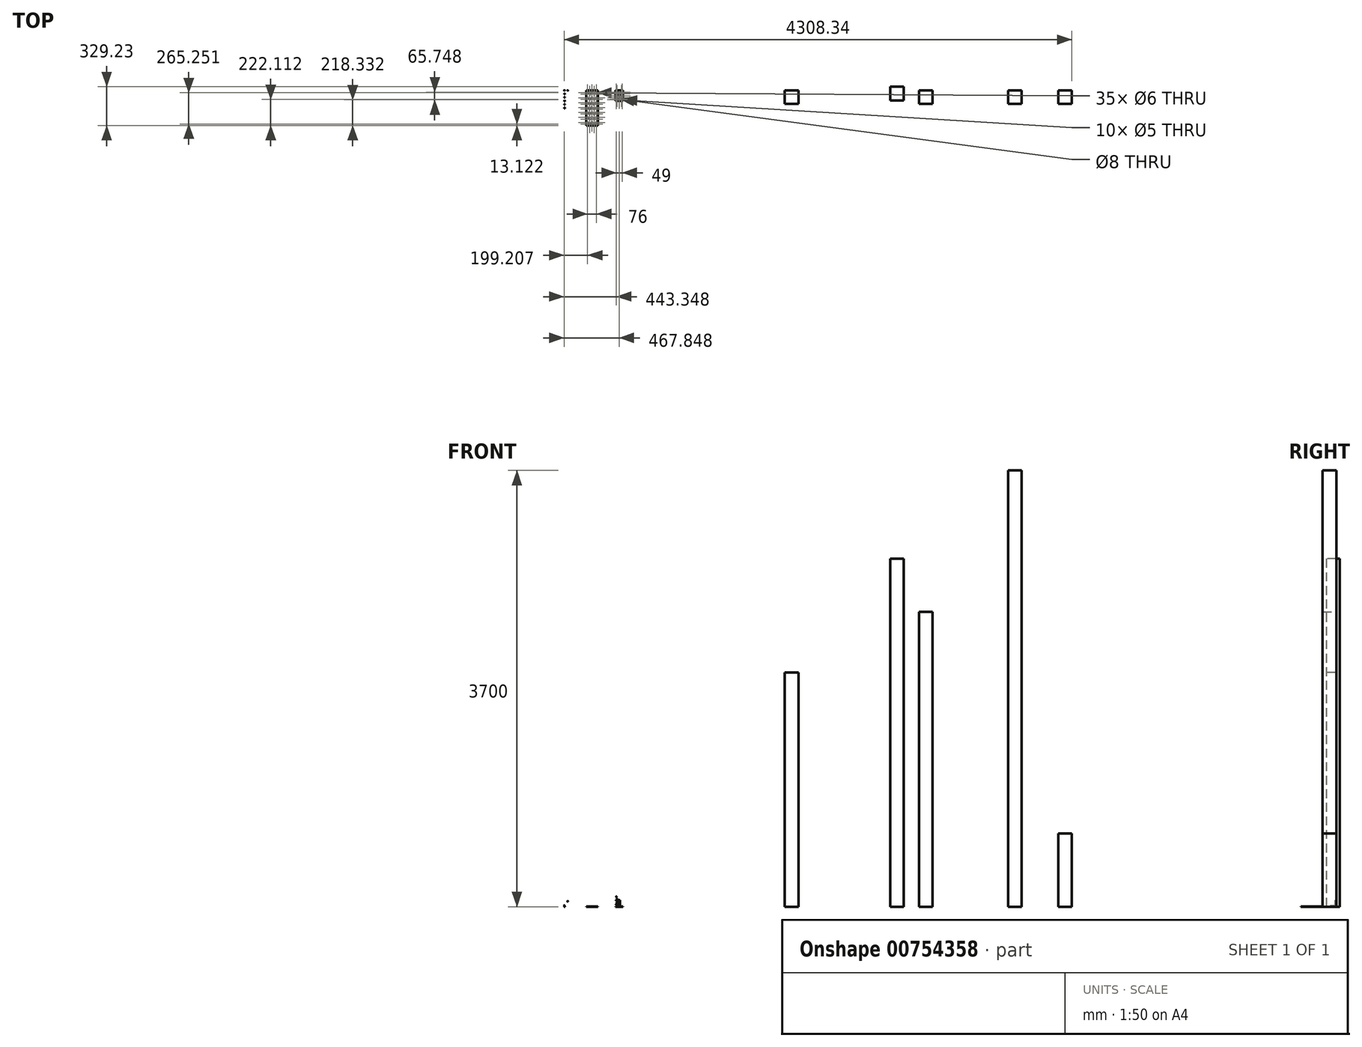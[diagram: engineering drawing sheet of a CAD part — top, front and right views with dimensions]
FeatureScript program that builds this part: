
annotation { "Feature Type Name" : "Feature", "Feature Type Description" : "" }
export const myFeature = defineFeature(function(context is Context, id is Id, definition is map)
    precondition{}
    {
        {
            var Q0;
            Q0=qCreatedBy(makeId("Top.planeOp"),FACE);
            var sketch = newSketch(context, id + "F0", { "sketchPlane" : qUnion([Q0])});
            skLineSegment(sketch, "E0.bottom", {"start": v(0, 0) * mm, "end": v(-115, 0) * mm});
            skLineSegment(sketch, "E0.top", {"start": v(0, -115) * mm, "end": v(-115, -115) * mm});
            skLineSegment(sketch, "E0.left", {"start": v(0, 0) * mm, "end": v(0, -115) * mm});
            skLineSegment(sketch, "E0.right", {"start": v(-115, 0) * mm, "end": v(-115, -115) * mm});
            skSolve(sketch);
        }
        {
            var Q0;
            Q0 = qSketchRegion(id + "F0", true);
            extrude(context, id + "F1", {"entities" : qUnion([Q0]), "depth" : 1985 * mm, "offsetDistance" : 25 * mm});
        }
        {
            var Q0;
            Q0=qCreatedBy(makeId("Top.planeOp"),FACE);
            var sketch = newSketch(context, id + "F2", { "sketchPlane" : qUnion([Q0])});
            skLineSegment(sketch, "E1.bottom", {"start": v(893.27, 29.23) * mm, "end": v(778.27, 29.23) * mm});
            skLineSegment(sketch, "E1.top", {"start": v(893.27, -85.77) * mm, "end": v(778.27, -85.77) * mm});
            skLineSegment(sketch, "E1.left", {"start": v(893.27, 29.23) * mm, "end": v(893.27, -85.77) * mm});
            skLineSegment(sketch, "E1.right", {"start": v(778.27, 29.23) * mm, "end": v(778.27, -85.77) * mm});
            skSolve(sketch);
        }
        {
            var Q0;
            Q0 = qSketchRegion(id + "F2", true);
            extrude(context, id + "F3", {"entities" : qUnion([Q0]), "depth" : 2950 * mm, "offsetDistance" : 25 * mm});
        }
        {
            var Q0;
            Q0=qCreatedBy(makeId("Top.planeOp"),FACE);
            var sketch = newSketch(context, id + "F4", { "sketchPlane" : qUnion([Q0])});
            skLineSegment(sketch, "E2.bottom", {"start": v(1022.34, -115) * mm, "end": v(1137.34, -115) * mm});
            skLineSegment(sketch, "E2.top", {"start": v(1022.34, 0) * mm, "end": v(1137.34, 0) * mm});
            skLineSegment(sketch, "E2.left", {"start": v(1022.34, -115) * mm, "end": v(1022.34, 0) * mm});
            skLineSegment(sketch, "E2.right", {"start": v(1137.34, -115) * mm, "end": v(1137.34, 0) * mm});
            skSolve(sketch);
        }
        {
            var Q0;
            Q0 = qSketchRegion(id + "F4", true);
            extrude(context, id + "F5", {"entities" : qUnion([Q0]), "depth" : 2500 * mm, "offsetDistance" : 25 * mm});
        }
        {
            var Q0;
            Q0=qCreatedBy(makeId("Top.planeOp"),FACE);
            var sketch = newSketch(context, id + "F6", { "sketchPlane" : qUnion([Q0])});
            skLineSegment(sketch, "E3.bottom", {"start": v(1892.32, 0) * mm, "end": v(1777.32, 0) * mm});
            skLineSegment(sketch, "E3.top", {"start": v(1892.32, -115) * mm, "end": v(1777.32, -115) * mm});
            skLineSegment(sketch, "E3.left", {"start": v(1892.32, 0) * mm, "end": v(1892.32, -115) * mm});
            skLineSegment(sketch, "E3.right", {"start": v(1777.32, 0) * mm, "end": v(1777.32, -115) * mm});
            skSolve(sketch);
        }
        {
            var Q0;
            Q0 = qSketchRegion(id + "F6", true);
            extrude(context, id + "F7", {"entities" : qUnion([Q0]), "depth" : 3700 * mm, "offsetDistance" : 25 * mm});
        }
        {
            var Q0;
            Q0=qCreatedBy(makeId("Top.planeOp"),FACE);
            var sketch = newSketch(context, id + "F8", { "sketchPlane" : qUnion([Q0])});
            skLineSegment(sketch, "E4.bottom", {"start": v(2205.3, 0) * mm, "end": v(2320.3, 0) * mm});
            skLineSegment(sketch, "E4.top", {"start": v(2205.3, -115) * mm, "end": v(2320.3, -115) * mm});
            skLineSegment(sketch, "E4.left", {"start": v(2205.3, 0) * mm, "end": v(2205.3, -115) * mm});
            skLineSegment(sketch, "E4.right", {"start": v(2320.3, 0) * mm, "end": v(2320.3, -115) * mm});
            skSolve(sketch);
        }
        {
            var Q0;
            Q0=makeQuery(id+"F8.imprint","IMPRINT",FACE,{"disambiguationData":[TD([[makeQuery(id+"F8.imprint","IMPRINT",EDGE,{"derivedFrom":sQuery(id+"F8.wireOp",EDGE,"E4.bottom")}),-1.0]])]});
            extrude(context, id + "F9", {"entities" : qUnion([Q0]), "depth" : 620 * mm, "offsetDistance" : 25 * mm});
        }
        {
            var Q0;
            Q0=qCreatedBy(makeId("Top.planeOp"),FACE);
            var sketch = newSketch(context, id + "F10", { "sketchPlane" : qUnion([Q0])});
            skLineSegment(sketch, "E5.bottom", {"start": v(-1487.68, 0) * mm, "end": v(-1552.68, 0) * mm});
            skLineSegment(sketch, "E5.top", {"start": v(-1487.68, -90) * mm, "end": v(-1552.68, -90) * mm});
            skLineSegment(sketch, "E5.left", {"start": v(-1487.68, 0) * mm, "end": v(-1487.68, -90) * mm});
            skLineSegment(sketch, "E5.right", {"start": v(-1552.68, 0) * mm, "end": v(-1552.68, -90) * mm});
            skCircle(sketch, "E6", {"center": v(-1520.18, -77.89) * mm, "radius": 4 * mm});
            skPoint(sketch, "E6.centerSnap0", {"position": v(-1520.18, -90) * mm});
            skLineSegment(sketch, "E7", {"start": v(-1544.68, -90) * mm, "end": v(-1544.68, 0) * mm, "construction": true});
            skLineSegment(sketch, "E8", {"start": v(-1539.68, -90) * mm, "end": v(-1539.68, 0) * mm, "construction": true});
            skLineSegment(sketch, "E9", {"start": v(-1520.18, 0) * mm, "end": v(-1520.18, -15.34) * mm, "construction": true});
            skCircle(sketch, "E10", {"center": v(-1544.68, -81.67) * mm, "radius": 2.5 * mm});
            skCircle(sketch, "E11", {"center": v(-1539.68, -63.63) * mm, "radius": 2.5 * mm});
            skCircle(sketch, "E12", {"center": v(-1544.68, -50.45) * mm, "radius": 2.5 * mm});
            skCircle(sketch, "E13", {"center": v(-1544.68, -15.92) * mm, "radius": 2.5 * mm});
            skCircle(sketch, "E14", {"center": v(-1539.68, -30.19) * mm, "radius": 2.5 * mm});
            skCircle(sketch, "E15.MirrorC", {"center": v(-1495.68, -15.92) * mm, "radius": 2.5 * mm});
            skCircle(sketch, "E16.MirrorC", {"center": v(-1500.68, -30.19) * mm, "radius": 2.5 * mm});
            skCircle(sketch, "E17.MirrorC", {"center": v(-1495.68, -50.45) * mm, "radius": 2.5 * mm});
            skCircle(sketch, "E18.MirrorC", {"center": v(-1500.68, -63.63) * mm, "radius": 2.5 * mm});
            skCircle(sketch, "E19.MirrorC", {"center": v(-1495.68, -81.67) * mm, "radius": 2.5 * mm});
            skSolve(sketch);
        }
        {
            var Q0;
            Q0=makeQuery(id+"F10.imprint","IMPRINT",FACE,{"disambiguationData":[TD([[makeQuery(id+"F10.imprint","IMPRINT",EDGE,{"derivedFrom":sQuery(id+"F10.wireOp",EDGE,"E5.bottom")}),1.0]])]});
            extrude(context, id + "F11", {"entities" : qUnion([Q0]), "depth" : 2.5 * mm, "offsetDistance" : 25 * mm});
        }
        {
            var Q0;
            Q0=makeQuery(id+"F11.opExtrude","CAP_FACE",FACE,{"disambiguationData":[OSD([sQuery(id+"F10.wireOp",EDGE,"E5.bottom"),sQuery(id+"F10.wireOp",EDGE,"E5.top"),sQuery(id+"F10.wireOp",EDGE,"E5.left"),sQuery(id+"F10.wireOp",EDGE,"E5.right")])],"isStart":false});
            var sketch = newSketch(context, id + "F12", { "sketchPlane" : qUnion([Q0])});
            skPoint(sketch, "E20", {"position": v(-1552.68, -2.5) * mm});
            skLineSegment(sketch, "E21", {"start": v(-1552.68, -2.5) * mm, "end": v(-1487.68, -2.5) * mm});
            skSolve(sketch);
        }
        {
            var Q0;
            Q0 = qSketchRegion(id + "F12", true);
            var Q1;
            {var subQ0=sQuery(id+"F12.wireOp",EDGE,"E21");Q1=makeQuery(id+"F12.imprint","IMPRINT",FACE,{"disambiguationData":[TD([[makeQuery(id+"F12.imprint","IMPRINT",EDGE,{"derivedFrom":subQ0}),1.0]])]});}
            extrude(context, id + "F13", {"entities" : qUnion([Q0, Q1]), "operationType" : NewBodyOperationType.ADD, "depth" : 90 * mm, "offsetDistance" : 25 * mm});
        }
        {
            var Q0;
            Q0=makeQuery(id+"F11.opExtrude","CAP_FACE",FACE,{"disambiguationData":[OSD([sQuery(id+"F10.wireOp",EDGE,"E5.bottom"),sQuery(id+"F10.wireOp",EDGE,"E5.top"),sQuery(id+"F10.wireOp",EDGE,"E5.left"),sQuery(id+"F10.wireOp",EDGE,"E5.right")])],"isStart":false});
            var sketch = newSketch(context, id + "F14", { "sketchPlane" : qUnion([Q0])});
            skLineSegment(sketch, "E22.bottom", {"start": v(-1520.18, -2.5) * mm, "end": v(-1527.18, -2.5) * mm});
            skLineSegment(sketch, "E22.top", {"start": v(-1520.18, -52.35) * mm, "end": v(-1527.18, -52.35) * mm});
            skLineSegment(sketch, "E22.left", {"start": v(-1520.18, -2.5) * mm, "end": v(-1520.18, -52.35) * mm, "construction": true});
            skLineSegment(sketch, "E22.right", {"start": v(-1527.18, -2.5) * mm, "end": v(-1527.18, -52.35) * mm});
            skLineSegment(sketch, "E23.bottom", {"start": v(-1520.18, -52.35) * mm, "end": v(-1513.18, -52.35) * mm});
            skLineSegment(sketch, "E23.top", {"start": v(-1520.18, -2.5) * mm, "end": v(-1513.18, -2.5) * mm});
            skLineSegment(sketch, "E23.left", {"start": v(-1520.18, -52.35) * mm, "end": v(-1520.18, -2.5) * mm});
            skLineSegment(sketch, "E23.right", {"start": v(-1513.18, -52.35) * mm, "end": v(-1513.18, -2.5) * mm});
            skSolve(sketch);
        }
        {
            var Q0;
            Q0=makeQuery(id+"F14.imprint","IMPRINT",FACE,{"disambiguationData":[TD([[makeQuery(id+"F14.imprint","IMPRINT",EDGE,{"derivedFrom":sQuery(id+"F14.wireOp",EDGE,"E23.bottom")}),1.0]])]});
            var Q1;
            Q1=makeQuery(id+"F14.imprint","IMPRINT",FACE,{"disambiguationData":[TD([[makeQuery(id+"F14.imprint","IMPRINT",EDGE,{"derivedFrom":sQuery(id+"F14.wireOp",EDGE,"E22.bottom")}),-1.0]])]});
            extrude(context, id + "F15", {"entities" : qUnion([Q0, Q1]), "operationType" : NewBodyOperationType.ADD, "depth" : 5 * mm, "offsetDistance" : 25 * mm});
        }
        {
            var Q0;
            Q0=makeQuery(id+"F13.opExtrude","SWEPT_FACE",FACE,{"disambiguationData":[OSD([sQuery(id+"F12.wireOp",EDGE,"E21")])]});
            var sketch = newSketch(context, id + "F16", { "sketchPlane" : qUnion([Q0])});
            skLineSegment(sketch, "E24", {"start": v(-1527.18, 7.5) * mm, "end": v(-1527.18, 57.5) * mm});
            skLineSegment(sketch, "E25", {"start": v(-1527.18, 57.5) * mm, "end": v(-1513.18, 57.5) * mm});
            skLineSegment(sketch, "E26", {"start": v(-1513.18, 57.5) * mm, "end": v(-1513.18, 7.5) * mm});
            skLineSegment(sketch, "E27", {"start": v(-1495.68, 92.82) * mm, "end": v(-1495.68, 2.82) * mm, "construction": true});
            skLineSegment(sketch, "E28", {"start": v(-1500.68, 92.82) * mm, "end": v(-1500.68, 2.82) * mm, "construction": true});
            skCircle(sketch, "E29", {"center": v(-1495.68, 84.49) * mm, "radius": 2.5 * mm});
            skCircle(sketch, "E30", {"center": v(-1500.68, 66.45) * mm, "radius": 2.5 * mm});
            skCircle(sketch, "E31", {"center": v(-1495.68, 53.27) * mm, "radius": 2.5 * mm});
            skCircle(sketch, "E32", {"center": v(-1495.68, 18.74) * mm, "radius": 2.5 * mm});
            skCircle(sketch, "E33", {"center": v(-1500.68, 33) * mm, "radius": 2.5 * mm});
            skLineSegment(sketch, "E34", {"start": v(-1520.18, 92.5) * mm, "end": v(-1520.18, 81.98) * mm, "construction": true});
            skCircle(sketch, "E35.MirrorC", {"center": v(-1544.68, 84.49) * mm, "radius": 2.5 * mm});
            skCircle(sketch, "E36.MirrorC", {"center": v(-1539.68, 66.45) * mm, "radius": 2.5 * mm});
            skCircle(sketch, "E37.MirrorC", {"center": v(-1544.68, 53.27) * mm, "radius": 2.5 * mm});
            skCircle(sketch, "E38.MirrorC", {"center": v(-1539.68, 33) * mm, "radius": 2.5 * mm});
            skCircle(sketch, "E39.MirrorC", {"center": v(-1544.68, 18.74) * mm, "radius": 2.5 * mm});
            skSolve(sketch);
        }
        {
            var Q0;
            Q0=makeQuery(id+"F16.imprint","IMPRINT",FACE,{"disambiguationData":[TD([[makeQuery(id+"F16.imprint","IMPRINT",EDGE,{"derivedFrom":sQuery(id+"F16.wireOp",EDGE,"E24")}),-1.0]])]});
            extrude(context, id + "F17", {"entities" : qUnion([Q0]), "operationType" : NewBodyOperationType.ADD, "depth" : 5 * mm, "offsetDistance" : 25 * mm});
        }
        {
            var Q0;
            Q0=makeQuery(id+"F17.opExtrude","CAP_EDGE",EDGE,{"disambiguationData":[OSD([sQuery(id+"F14.wireOp",EDGE,"E22.bottom"),sQuery(id+"F14.wireOp",EDGE,"E23.top")])],"isStart":false});
            var Q1;
            Q1=makeQuery(id+"F15.opExtrude","CAP_EDGE",EDGE,{"disambiguationData":[OSD([sQuery(id+"F14.wireOp",EDGE,"E22.right")])],"isStart":false});
            var Q2;
            Q2=makeQuery(id+"F17.opExtrude","CAP_EDGE",EDGE,{"disambiguationData":[OSD([sQuery(id+"F16.wireOp",EDGE,"E26")])],"isStart":false});
            var Q3;
            Q3=makeQuery(id+"F15.opExtrude","CAP_EDGE",EDGE,{"disambiguationData":[OSD([sQuery(id+"F14.wireOp",EDGE,"E22.top"),sQuery(id+"F14.wireOp",EDGE,"E23.bottom")])],"isStart":false});
            var Q4;
            Q4=makeQuery(id+"F17.opExtrude","CAP_EDGE",EDGE,{"disambiguationData":[OSD([sQuery(id+"F16.wireOp",EDGE,"E25")])],"isStart":false});
            fillet(context, id + "F18", {"entities" : qUnion([Q0, Q1, Q2, Q3, Q4]), "radius" : 5 * mm, "tangentPropagation" : true, "allowEdgeOverflow" : false});
        }
        {
            var Q0;
            Q0=makeQuery(id+"F16.imprint","IMPRINT",FACE,{"disambiguationData":[TD([[makeQuery(id+"F16.imprint","IMPRINT",EDGE,{"derivedFrom":sQuery(id+"F16.wireOp",EDGE,"E39.MirrorC")}),-1.0]])]});
            var Q1;
            Q1=makeQuery(id+"F16.imprint","IMPRINT",FACE,{"disambiguationData":[TD([[makeQuery(id+"F16.imprint","IMPRINT",EDGE,{"derivedFrom":sQuery(id+"F16.wireOp",EDGE,"E38.MirrorC")}),-1.0]])]});
            var Q2;
            Q2=makeQuery(id+"F16.imprint","IMPRINT",FACE,{"disambiguationData":[TD([[makeQuery(id+"F16.imprint","IMPRINT",EDGE,{"derivedFrom":sQuery(id+"F16.wireOp",EDGE,"E37.MirrorC")}),-1.0]])]});
            var Q3;
            Q3=makeQuery(id+"F16.imprint","IMPRINT",FACE,{"disambiguationData":[TD([[makeQuery(id+"F16.imprint","IMPRINT",EDGE,{"derivedFrom":sQuery(id+"F16.wireOp",EDGE,"E36.MirrorC")}),-1.0]])]});
            var Q4;
            Q4=makeQuery(id+"F16.imprint","IMPRINT",FACE,{"disambiguationData":[TD([[makeQuery(id+"F16.imprint","IMPRINT",EDGE,{"derivedFrom":sQuery(id+"F16.wireOp",EDGE,"E35.MirrorC")}),-1.0]])]});
            var Q5;
            Q5=makeQuery(id+"F16.imprint","IMPRINT",FACE,{"disambiguationData":[TD([[makeQuery(id+"F16.imprint","IMPRINT",EDGE,{"derivedFrom":sQuery(id+"F16.wireOp",EDGE,"E29")}),1.0]])]});
            var Q6;
            Q6=makeQuery(id+"F16.imprint","IMPRINT",FACE,{"disambiguationData":[TD([[makeQuery(id+"F16.imprint","IMPRINT",EDGE,{"derivedFrom":sQuery(id+"F16.wireOp",EDGE,"E30")}),1.0]])]});
            var Q7;
            Q7=makeQuery(id+"F16.imprint","IMPRINT",FACE,{"disambiguationData":[TD([[makeQuery(id+"F16.imprint","IMPRINT",EDGE,{"derivedFrom":sQuery(id+"F16.wireOp",EDGE,"E31")}),1.0]])]});
            var Q8;
            Q8=makeQuery(id+"F16.imprint","IMPRINT",FACE,{"disambiguationData":[TD([[makeQuery(id+"F16.imprint","IMPRINT",EDGE,{"derivedFrom":sQuery(id+"F16.wireOp",EDGE,"E33")}),1.0]])]});
            var Q9;
            Q9=makeQuery(id+"F16.imprint","IMPRINT",FACE,{"disambiguationData":[TD([[makeQuery(id+"F16.imprint","IMPRINT",EDGE,{"derivedFrom":sQuery(id+"F16.wireOp",EDGE,"E32")}),1.0]])]});
            extrude(context, id + "F19", {"entities" : qUnion([Q0, Q1, Q2, Q3, Q4, Q5, Q6, Q7, Q8, Q9]), "operationType" : NewBodyOperationType.REMOVE, "oppositeDirection" : true, "depth" : 25 * mm, "offsetDistance" : 25 * mm});
        }
        {
            var Q0;
            Q0=qCreatedBy(makeId("Top.planeOp"),FACE);
            var sketch = newSketch(context, id + "F20", { "sketchPlane" : qUnion([Q0])});
            skLineSegment(sketch, "E40.bottom", {"start": v(-1700.82, 0) * mm, "end": v(-1800.82, 0) * mm});
            skLineSegment(sketch, "E40.top", {"start": v(-1700.82, -300) * mm, "end": v(-1800.82, -300) * mm});
            skLineSegment(sketch, "E40.left", {"start": v(-1700.82, 0) * mm, "end": v(-1700.82, -300) * mm});
            skLineSegment(sketch, "E40.right", {"start": v(-1800.82, 0) * mm, "end": v(-1800.82, -300) * mm});
            skLineSegment(sketch, "E41", {"start": v(-1788.82, -300) * mm, "end": v(-1788.82, 0) * mm, "construction": true});
            skLineSegment(sketch, "E42.1.0.0", {"start": v(-1769.82, -300) * mm, "end": v(-1769.82, 0) * mm, "construction": true});
            skLineSegment(sketch, "E42.2.0.0", {"start": v(-1750.82, -300) * mm, "end": v(-1750.82, 0) * mm, "construction": true});
            skLineSegment(sketch, "E42.3.0.0", {"start": v(-1731.82, -300) * mm, "end": v(-1731.82, 0) * mm, "construction": true});
            skLineSegment(sketch, "E42.4.0.0", {"start": v(-1712.82, -300) * mm, "end": v(-1712.82, 0) * mm, "construction": true});
            skLineSegment(sketch, "E42.direction1", {"start": v(-1788.82, -300) * mm, "end": v(-1769.82, -300) * mm, "construction": true});
            skCircle(sketch, "E43", {"center": v(-1769.82, -286.88) * mm, "radius": 3 * mm});
            skCircle(sketch, "E44", {"center": v(-1731.82, -286.88) * mm, "radius": 3 * mm});
            skCircle(sketch, "E45", {"center": v(-1788.82, -273.63) * mm, "radius": 3 * mm});
            skCircle(sketch, "E46", {"center": v(-1750.82, -273.63) * mm, "radius": 3 * mm});
            skCircle(sketch, "E47", {"center": v(-1712.82, -273.63) * mm, "radius": 3 * mm});
            skCircle(sketch, "E48.0.1.0", {"center": v(-1788.82, -231.63) * mm, "radius": 3 * mm});
            skCircle(sketch, "E48.0.1.1", {"center": v(-1769.82, -244.88) * mm, "radius": 3 * mm});
            skCircle(sketch, "E48.0.1.2", {"center": v(-1750.82, -231.63) * mm, "radius": 3 * mm});
            skCircle(sketch, "E48.0.1.3", {"center": v(-1731.82, -244.88) * mm, "radius": 3 * mm});
            skCircle(sketch, "E48.0.1.4", {"center": v(-1712.82, -231.63) * mm, "radius": 3 * mm});
            skCircle(sketch, "E48.0.2.0", {"center": v(-1788.82, -189.63) * mm, "radius": 3 * mm});
            skCircle(sketch, "E48.0.2.1", {"center": v(-1769.82, -202.88) * mm, "radius": 3 * mm});
            skCircle(sketch, "E48.0.2.2", {"center": v(-1750.82, -189.63) * mm, "radius": 3 * mm});
            skCircle(sketch, "E48.0.2.3", {"center": v(-1731.82, -202.88) * mm, "radius": 3 * mm});
            skCircle(sketch, "E48.0.2.4", {"center": v(-1712.82, -189.63) * mm, "radius": 3 * mm});
            skCircle(sketch, "E48.0.3.0", {"center": v(-1788.82, -147.63) * mm, "radius": 3 * mm});
            skCircle(sketch, "E48.0.3.1", {"center": v(-1769.82, -160.88) * mm, "radius": 3 * mm});
            skCircle(sketch, "E48.0.3.2", {"center": v(-1750.82, -147.63) * mm, "radius": 3 * mm});
            skCircle(sketch, "E48.0.3.3", {"center": v(-1731.82, -160.88) * mm, "radius": 3 * mm});
            skCircle(sketch, "E48.0.3.4", {"center": v(-1712.82, -147.63) * mm, "radius": 3 * mm});
            skCircle(sketch, "E48.0.4.0", {"center": v(-1788.82, -105.63) * mm, "radius": 3 * mm});
            skCircle(sketch, "E48.0.4.1", {"center": v(-1769.82, -118.88) * mm, "radius": 3 * mm});
            skCircle(sketch, "E48.0.4.2", {"center": v(-1750.82, -105.63) * mm, "radius": 3 * mm});
            skCircle(sketch, "E48.0.4.3", {"center": v(-1731.82, -118.88) * mm, "radius": 3 * mm});
            skCircle(sketch, "E48.0.4.4", {"center": v(-1712.82, -105.63) * mm, "radius": 3 * mm});
            skCircle(sketch, "E48.0.5.0", {"center": v(-1788.82, -63.63) * mm, "radius": 3 * mm});
            skCircle(sketch, "E48.0.5.1", {"center": v(-1769.82, -76.88) * mm, "radius": 3 * mm});
            skCircle(sketch, "E48.0.5.2", {"center": v(-1750.82, -63.63) * mm, "radius": 3 * mm});
            skCircle(sketch, "E48.0.5.3", {"center": v(-1731.82, -76.88) * mm, "radius": 3 * mm});
            skCircle(sketch, "E48.0.5.4", {"center": v(-1712.82, -63.63) * mm, "radius": 3 * mm});
            skCircle(sketch, "E48.0.6.0", {"center": v(-1788.82, -21.63) * mm, "radius": 3 * mm});
            skCircle(sketch, "E48.0.6.1", {"center": v(-1769.82, -34.88) * mm, "radius": 3 * mm});
            skCircle(sketch, "E48.0.6.2", {"center": v(-1750.82, -21.63) * mm, "radius": 3 * mm});
            skCircle(sketch, "E48.0.6.3", {"center": v(-1731.82, -34.88) * mm, "radius": 3 * mm});
            skCircle(sketch, "E48.0.6.4", {"center": v(-1712.82, -21.63) * mm, "radius": 3 * mm});
            skLineSegment(sketch, "E48.direction1", {"start": v(-1788.82, -273.63) * mm, "end": v(-1763.82, -273.63) * mm, "construction": true});
            skLineSegment(sketch, "E48.direction2", {"start": v(-1788.82, -273.63) * mm, "end": v(-1788.82, -231.63) * mm, "construction": true});
            skSolve(sketch);
        }
        {
            var Q0;
            Q0=makeQuery(id+"F20.imprint","IMPRINT",FACE,{"disambiguationData":[TD([[makeQuery(id+"F20.imprint","IMPRINT",EDGE,{"derivedFrom":sQuery(id+"F20.wireOp",EDGE,"E40.bottom")}),1.0]])]});
            extrude(context, id + "F21", {"entities" : qUnion([Q0]), "depth" : 2 * mm, "offsetDistance" : 25 * mm});
        }
        {
            var Q0;
            Q0=qCreatedBy(makeId("Top.planeOp"),FACE);
            var sketch = newSketch(context, id + "F22", { "sketchPlane" : qUnion([Q0])});
            skLineSegment(sketch, "E49.bottom", {"start": v(-1951.4, 0) * mm, "end": v(-1991.4, 0) * mm});
            skLineSegment(sketch, "E49.top", {"start": v(-1951.4, -160) * mm, "end": v(-1991.4, -160) * mm});
            skLineSegment(sketch, "E49.left", {"start": v(-1951.4, 0) * mm, "end": v(-1951.4, -160) * mm});
            skLineSegment(sketch, "E49.right", {"start": v(-1991.4, 0) * mm, "end": v(-1991.4, -160) * mm});
            skSolve(sketch);
        }
        {
            var Q0;
            Q0=makeQuery(id+"F22.imprint","IMPRINT",FACE,{"disambiguationData":[TD([[makeQuery(id+"F22.imprint","IMPRINT",EDGE,{"derivedFrom":sQuery(id+"F22.wireOp",EDGE,"E49.bottom")}),1.0]])]});
            extrude(context, id + "F23", {"entities" : qUnion([Q0]), "depth" : 3 * mm, "offsetDistance" : 25 * mm});
        }
        {
            var Q0;
            Q0=makeQuery(id+"F23.opExtrude","CAP_FACE",FACE,{"disambiguationData":[OSD([sQuery(id+"F22.wireOp",EDGE,"E49.bottom"),sQuery(id+"F22.wireOp",EDGE,"E49.top"),sQuery(id+"F22.wireOp",EDGE,"E49.left"),sQuery(id+"F22.wireOp",EDGE,"E49.right")])],"isStart":false});
            var sketch = newSketch(context, id + "F24", { "sketchPlane" : qUnion([Q0])});
            skLineSegment(sketch, "E50", {"start": v(-1991.4, -3) * mm, "end": v(-1951.4, -3) * mm});
            skSolve(sketch);
        }
        {
            var Q0;
            {var subQ0=sQuery(id+"F24.wireOp",EDGE,"E50");Q0=makeQuery(id+"F24.imprint","IMPRINT",FACE,{"disambiguationData":[TD([[makeQuery(id+"F24.imprint","IMPRINT",EDGE,{"derivedFrom":subQ0}),1.0]])]});}
            extrude(context, id + "F25", {"entities" : qUnion([Q0]), "operationType" : NewBodyOperationType.ADD, "depth" : 50 * mm, "offsetDistance" : 25 * mm});
        }
        {
            var Q0;
            Q0=makeQuery(id+"F25.opExtrude","SWEPT_FACE",FACE,{"disambiguationData":[OSD([sQuery(id+"F24.wireOp",EDGE,"E50")])]});
            var sketch = newSketch(context, id + "F26", { "sketchPlane" : qUnion([Q0])});
            skLineSegment(sketch, "E51", {"start": v(-1951.4, 3) * mm, "end": v(-1991.4, 53) * mm, "construction": true});
            skCircle(sketch, "E52", {"center": v(-1971.4, 28) * mm, "radius": 5 * mm});
            skCircle(sketch, "E53", {"center": v(-1985.53, 45.65) * mm, "radius": 2.5 * mm});
            skLineSegment(sketch, "E54", {"start": v(-1971.4, 53) * mm, "end": v(-1971.4, 46.14) * mm});
            skLineSegment(sketch, "E55", {"start": v(-1991.4, 28) * mm, "end": v(-1987.03, 28) * mm});
            skCircle(sketch, "E56.MirrorC", {"center": v(-1957.29, 45.65) * mm, "radius": 2.5 * mm});
            skCircle(sketch, "E57.MirrorC", {"center": v(-1985.53, 10.35) * mm, "radius": 2.5 * mm});
            skCircle(sketch, "E58.MirrorC", {"center": v(-1957.29, 10.35) * mm, "radius": 2.5 * mm});
            skSolve(sketch);
        }
        {
            var Q0;
            Q0=makeQuery(id+"F26.imprint","IMPRINT",FACE,{"disambiguationData":[TD([[makeQuery(id+"F26.imprint","IMPRINT",EDGE,{"derivedFrom":sQuery(id+"F26.wireOp",EDGE,"E52")}),1.0]])]});
            var Q1;
            Q1=makeQuery(id+"F26.imprint","IMPRINT",FACE,{"disambiguationData":[TD([[makeQuery(id+"F26.imprint","IMPRINT",EDGE,{"derivedFrom":sQuery(id+"F26.wireOp",EDGE,"E57.MirrorC")}),-1.0]])]});
            var Q2;
            Q2=makeQuery(id+"F26.imprint","IMPRINT",FACE,{"disambiguationData":[TD([[makeQuery(id+"F26.imprint","IMPRINT",EDGE,{"derivedFrom":sQuery(id+"F26.wireOp",EDGE,"E53")}),1.0]])]});
            var Q3;
            Q3=makeQuery(id+"F26.imprint","IMPRINT",FACE,{"disambiguationData":[TD([[makeQuery(id+"F26.imprint","IMPRINT",EDGE,{"derivedFrom":sQuery(id+"F26.wireOp",EDGE,"E56.MirrorC")}),-1.0]])]});
            var Q4;
            Q4=makeQuery(id+"F26.imprint","IMPRINT",FACE,{"disambiguationData":[TD([[makeQuery(id+"F26.imprint","IMPRINT",EDGE,{"derivedFrom":sQuery(id+"F26.wireOp",EDGE,"E58.MirrorC")}),1.0]])]});
            extrude(context, id + "F27", {"entities" : qUnion([Q0, Q1, Q2, Q3, Q4]), "operationType" : NewBodyOperationType.REMOVE, "oppositeDirection" : true, "depth" : 25 * mm, "offsetDistance" : 25 * mm});
        }
        {
            var Q0;
            Q0=makeQuery(id+"F25.opExtrude","CAP_EDGE",EDGE,{"disambiguationData":[OSD([sQuery(id+"F24.wireOp",EDGE,"E50")])],"isStart":true});
            var Q1;
            Q1=makeQuery(id+"F23.opExtrude","CAP_EDGE",EDGE,{"disambiguationData":[OSD([sQuery(id+"F22.wireOp",EDGE,"E49.bottom")])],"isStart":true});
            fillet(context, id + "F28", {"entities" : qUnion([Q0, Q1]), "radius" : 2 * mm, "tangentPropagation" : true, "allowEdgeOverflow" : false});
        }
        {
            var Q0;
            Q0=makeQuery(id+"F23.opExtrude","CAP_FACE",FACE,{"disambiguationData":[OSD([sQuery(id+"F22.wireOp",EDGE,"E49.bottom"),sQuery(id+"F22.wireOp",EDGE,"E49.top"),sQuery(id+"F22.wireOp",EDGE,"E49.left"),sQuery(id+"F22.wireOp",EDGE,"E49.right")])],"isStart":false});
            var sketch = newSketch(context, id + "F29", { "sketchPlane" : qUnion([Q0])});
            skLineSegment(sketch, "E59", {"start": v(-1971.4, -160) * mm, "end": v(-1971.4, -5) * mm, "construction": true});
            skCircle(sketch, "E60", {"center": v(-1971.4, -47.72) * mm, "radius": 5 * mm});
            skCircle(sketch, "E61", {"center": v(-1971.4, -105.83) * mm, "radius": 5 * mm});
            skLineSegment(sketch, "E62", {"start": v(-1959.4, -160) * mm, "end": v(-1959.4, -5) * mm, "construction": true});
            skCircle(sketch, "E63", {"center": v(-1959.4, -150.96) * mm, "radius": 2.5 * mm});
            skCircle(sketch, "E64.0.1.0", {"center": v(-1959.4, -120.96) * mm, "radius": 2.5 * mm});
            skCircle(sketch, "E64.0.2.0", {"center": v(-1959.4, -90.96) * mm, "radius": 2.5 * mm});
            skCircle(sketch, "E64.0.3.0", {"center": v(-1959.4, -60.96) * mm, "radius": 2.5 * mm});
            skCircle(sketch, "E64.0.4.0", {"center": v(-1959.4, -30.96) * mm, "radius": 2.5 * mm});
            skLineSegment(sketch, "E64.direction1", {"start": v(-1959.4, -150.96) * mm, "end": v(-1934.4, -150.96) * mm, "construction": true});
            skLineSegment(sketch, "E64.direction2", {"start": v(-1959.4, -150.96) * mm, "end": v(-1959.4, -120.96) * mm, "construction": true});
            skCircle(sketch, "E65.MirrorC", {"center": v(-1983.4, -90.96) * mm, "radius": 2.5 * mm});
            skCircle(sketch, "E66.MirrorC", {"center": v(-1983.4, -60.96) * mm, "radius": 2.5 * mm});
            skCircle(sketch, "E67.MirrorC", {"center": v(-1983.4, -30.96) * mm, "radius": 2.5 * mm});
            skCircle(sketch, "E68.MirrorC", {"center": v(-1983.4, -120.96) * mm, "radius": 2.5 * mm});
            skCircle(sketch, "E69.MirrorC", {"center": v(-1983.4, -150.96) * mm, "radius": 2.5 * mm});
            skSolve(sketch);
        }
        {
            var Q0;
            Q0=makeQuery(id+"F29.imprint","IMPRINT",FACE,{"disambiguationData":[TD([[makeQuery(id+"F29.imprint","IMPRINT",EDGE,{"derivedFrom":sQuery(id+"F29.wireOp",EDGE,"E64.0.4.0")}),1.0]])]});
            var Q1;
            Q1=makeQuery(id+"F29.imprint","IMPRINT",FACE,{"disambiguationData":[TD([[makeQuery(id+"F29.imprint","IMPRINT",EDGE,{"derivedFrom":sQuery(id+"F29.wireOp",EDGE,"E64.0.3.0")}),1.0]])]});
            var Q2;
            Q2=makeQuery(id+"F29.imprint","IMPRINT",FACE,{"disambiguationData":[TD([[makeQuery(id+"F29.imprint","IMPRINT",EDGE,{"derivedFrom":sQuery(id+"F29.wireOp",EDGE,"E64.0.2.0")}),1.0]])]});
            var Q3;
            Q3=makeQuery(id+"F29.imprint","IMPRINT",FACE,{"disambiguationData":[TD([[makeQuery(id+"F29.imprint","IMPRINT",EDGE,{"derivedFrom":sQuery(id+"F29.wireOp",EDGE,"E64.0.1.0")}),1.0]])]});
            var Q4;
            Q4=makeQuery(id+"F29.imprint","IMPRINT",FACE,{"disambiguationData":[TD([[makeQuery(id+"F29.imprint","IMPRINT",EDGE,{"derivedFrom":sQuery(id+"F29.wireOp",EDGE,"E63")}),1.0]])]});
            var Q5;
            Q5=makeQuery(id+"F29.imprint","IMPRINT",FACE,{"disambiguationData":[TD([[makeQuery(id+"F29.imprint","IMPRINT",EDGE,{"derivedFrom":sQuery(id+"F29.wireOp",EDGE,"E69.MirrorC")}),-1.0]])]});
            var Q6;
            Q6=makeQuery(id+"F29.imprint","IMPRINT",FACE,{"disambiguationData":[TD([[makeQuery(id+"F29.imprint","IMPRINT",EDGE,{"derivedFrom":sQuery(id+"F29.wireOp",EDGE,"E68.MirrorC")}),-1.0]])]});
            var Q7;
            Q7=makeQuery(id+"F29.imprint","IMPRINT",FACE,{"disambiguationData":[TD([[makeQuery(id+"F29.imprint","IMPRINT",EDGE,{"derivedFrom":sQuery(id+"F29.wireOp",EDGE,"E65.MirrorC")}),-1.0]])]});
            var Q8;
            Q8=makeQuery(id+"F29.imprint","IMPRINT",FACE,{"disambiguationData":[TD([[makeQuery(id+"F29.imprint","IMPRINT",EDGE,{"derivedFrom":sQuery(id+"F29.wireOp",EDGE,"E66.MirrorC")}),-1.0]])]});
            var Q9;
            Q9=makeQuery(id+"F29.imprint","IMPRINT",FACE,{"disambiguationData":[TD([[makeQuery(id+"F29.imprint","IMPRINT",EDGE,{"derivedFrom":sQuery(id+"F29.wireOp",EDGE,"E67.MirrorC")}),-1.0]])]});
            var Q10;
            Q10=makeQuery(id+"F29.imprint","IMPRINT",FACE,{"disambiguationData":[TD([[makeQuery(id+"F29.imprint","IMPRINT",EDGE,{"derivedFrom":sQuery(id+"F29.wireOp",EDGE,"E60")}),1.0]])]});
            var Q11;
            Q11=makeQuery(id+"F29.imprint","IMPRINT",FACE,{"disambiguationData":[TD([[makeQuery(id+"F29.imprint","IMPRINT",EDGE,{"derivedFrom":sQuery(id+"F29.wireOp",EDGE,"E61")}),1.0]])]});
            extrude(context, id + "F30", {"entities" : qUnion([Q0, Q1, Q2, Q3, Q4, Q5, Q6, Q7, Q8, Q9, Q10, Q11]), "operationType" : NewBodyOperationType.REMOVE, "oppositeDirection" : true, "depth" : 25 * mm, "offsetDistance" : 25 * mm});
        }
    });
